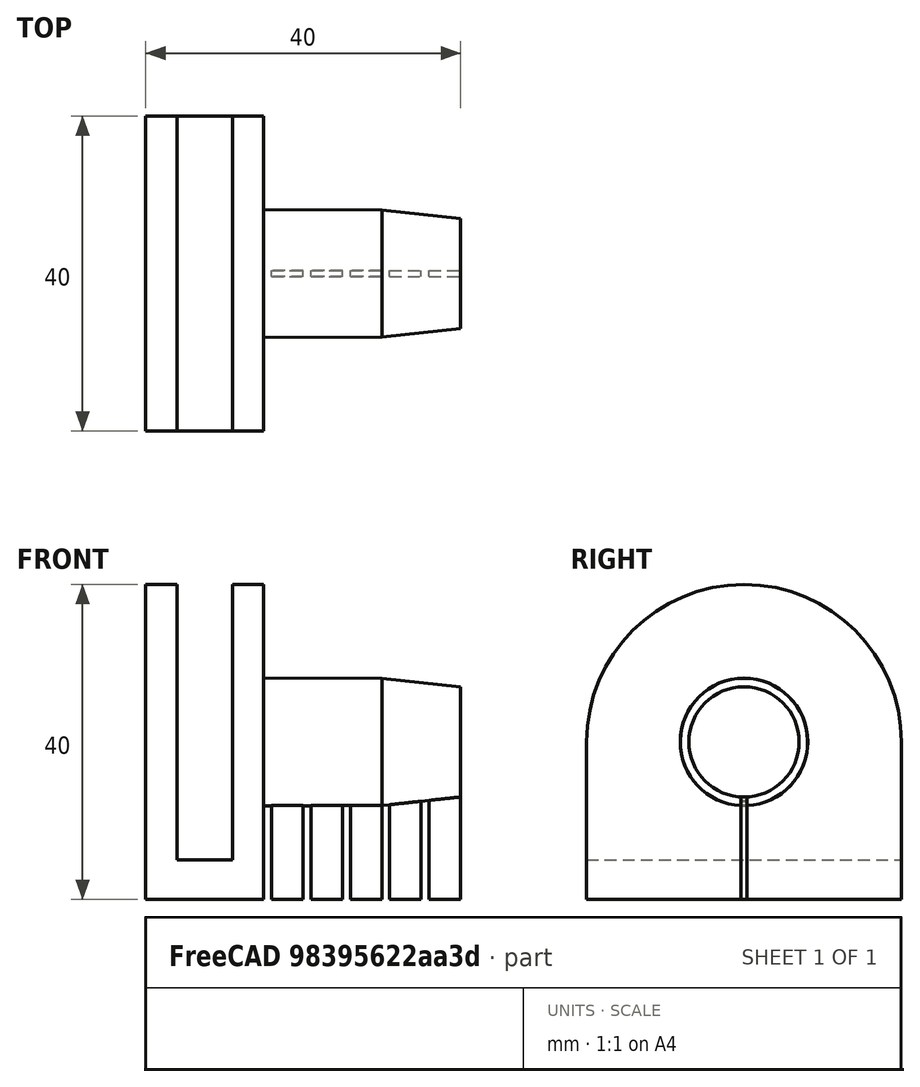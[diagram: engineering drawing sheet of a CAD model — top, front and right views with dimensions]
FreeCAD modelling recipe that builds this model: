
FCSTD DOCUMENT  (FreeCAD 0.14R2771 (Git))
Label: douche01
License: CC-BY 3.0
LicenseURL: http://creativecommons.org/licenses/by/3.0/
objects: Part::Fuse×8, Part::Box×7, Part::Cone×2, Part::Cylinder×1, Part::Cut×1
note: 19 computed .brp shape members not serialized (recipe doc carries the construction recipe); baked Part::Feature solids carry a one-line shape summary decoded from their .brp

FEATURE [Part::Box] Box  label="Box-corps"
  Height = 15
  Length = 20
  Placement = pos=(0,-20,0) rot=(0,0,1;0rad)
  Width = 40
FEATURE [Part::Cylinder] Cylinder001  label="Cylinder-corps"
  Angle = 360
  Height = 15
  Radius = 20
FEATURE [Part::Box] Box001  label="trou"
  Height = 7
  Length = 36
  Placement = pos=(-21,-23,4) rot=(0,0,1;0rad)
  Width = 46
FEATURE [Part::Cone] Cone001
  Angle = 360
  Height = 10
  Placement = pos=(0,0,30) rot=(0,0,1;0rad)
  Radius1 = 8.09
  Radius2 = 7
FEATURE [Part::Cone] Cone
  Angle = 360
  Height = 15
  Placement = pos=(0,0,15) rot=(0,0,1;0rad)
  Radius1 = 8.1
  Radius2 = 8.09
FEATURE [Part::Fuse] Fusion
  Base = -> Box
  Tool = -> Cylinder001
FEATURE [Part::Cut] Cut  label="Corps"
  Base = -> Fusion
  Tool = -> Box001
FEATURE [Part::Fuse] Fusion001  label="Prise male"
  Base = -> Cone
  Tool = -> Cone001
FEATURE [Part::Fuse] Fusion002  label="Connecteur"
  Base = -> Cut
  Placement = pos=(0,0,0) rot=(0,1,0;1.5708rad)
  Tool = -> Fusion001
FEATURE [Part::Box] Box002  label="Support01"
  Height = 13
  Length = 4
  Placement = pos=(16,-0.4,-20) rot=(0,0,1;0rad)
  Width = 0.8
FEATURE [Part::Box] Box002001  label="Support002"
  Height = 13
  Length = 4
  Placement = pos=(21,-0.4,-20) rot=(0,0,1;0rad)
  Width = 0.8
FEATURE [Part::Box] Box002002  label="Support003"
  Height = 13
  Length = 4
  Placement = pos=(26,-0.4,-20) rot=(0,0,1;0rad)
  Width = 0.8
FEATURE [Part::Box] Box002003  label="Support004"
  Height = 13
  Length = 4
  Placement = pos=(31,-0.4,-20) rot=(0,0,1;0rad)
  Width = 0.8
FEATURE [Part::Box] Box002004  label="Support005"
  Height = 13
  Length = 4
  Placement = pos=(36,-0.4,-20) rot=(0,0,1;0rad)
  Width = 0.8
FEATURE [Part::Fuse] Fusion003
  Base = -> Box002
  Tool = -> Box002001
FEATURE [Part::Fuse] Fusion004
  Base = -> Fusion003
  Tool = -> Box002002
FEATURE [Part::Fuse] Fusion005
  Base = -> Fusion004
  Tool = -> Box002003
FEATURE [Part::Fuse] Fusion006  label="Support"
  Base = -> Fusion005
  Tool = -> Box002004
FEATURE [Part::Fuse] Fusion007  label="Connecteur et support"
  Base = -> Fusion002
  Tool = -> Fusion006
